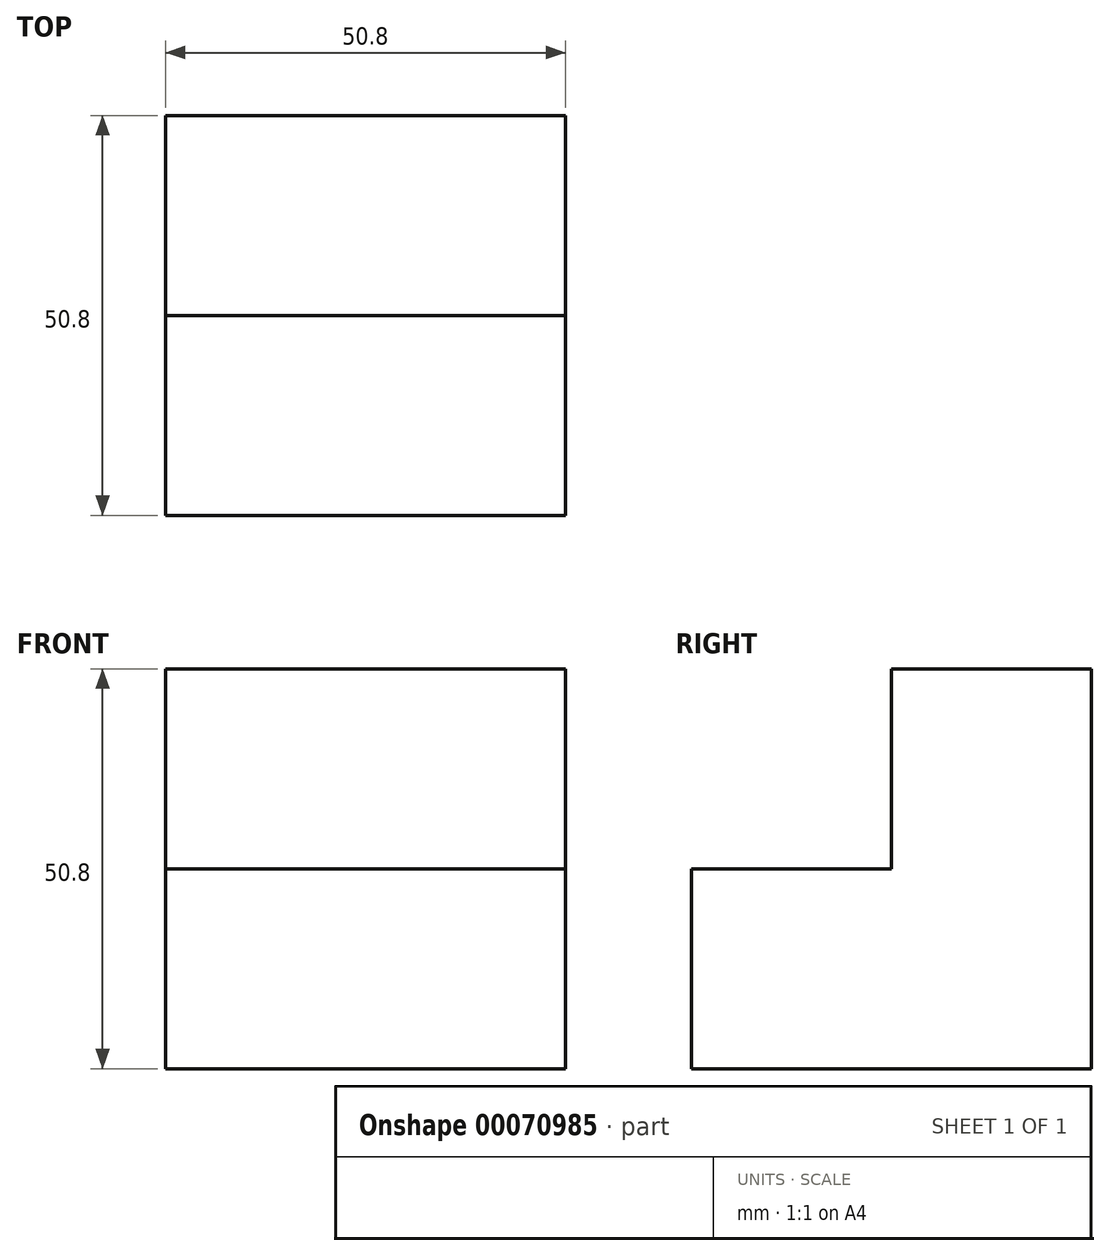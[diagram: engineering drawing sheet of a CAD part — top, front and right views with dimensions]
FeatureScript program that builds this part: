
annotation { "Feature Type Name" : "Feature", "Feature Type Description" : "" }
export const myFeature = defineFeature(function(context is Context, id is Id, definition is map)
    precondition{}
    {
        {
            var Q0;
            Q0=qCreatedBy(makeId("Right.planeOp"),FACE);
            var sketch = newSketch(context, id + "F0", { "sketchPlane" : qUnion([Q0])});
            skLineSegment(sketch, "E0", {"start": v(14.23, 23.86) * mm, "end": v(14.23, -26.94) * mm});
            skLineSegment(sketch, "E1", {"start": v(14.23, -26.94) * mm, "end": v(-36.57, -26.94) * mm});
            skLineSegment(sketch, "E2", {"start": v(-36.57, -26.94) * mm, "end": v(-36.57, -1.54) * mm});
            skLineSegment(sketch, "E3", {"start": v(-36.57, -1.54) * mm, "end": v(-11.17, -1.54) * mm});
            skLineSegment(sketch, "E4", {"start": v(-11.17, -1.54) * mm, "end": v(-11.17, 23.86) * mm});
            skLineSegment(sketch, "E5", {"start": v(-11.17, 23.86) * mm, "end": v(14.23, 23.86) * mm});
            skSolve(sketch);
        }
        {
            var Q0;
            Q0 = qSketchRegion(id + "F0", true);
            extrude(context, id + "F1", {"entities" : qUnion([Q0]), "depth" : 50.8 * mm});
        }
    });
